# Revit family: pascala_round_901803_004_1_f1d9
name_source: partatom
category: Lighting Fixtures
units: mm (PartAtom-declared; Revit-internal decimal feet)

## family parameters
Cut with Voids When Loaded = No
Host = Face
Light Source = No
Part Type = Normal
Room Calculation Point = No
Round Connector Dimension = Use Diameter
Shared = No

## types (1)
- MultiLumen 1 (1 x LED Modul 940, 1700 lm, 4000)
    Apparent Load = 11 VA
    Approval mark = CE
    CIE Flux Codes = 95 100 100 100 100
    Color Rendering = 92
    Color Temperature = 4000
    Default Elevation = 1800 mm
    Description = Series: PASCALA round
High quality recessed downlight. Mounting bracket: galvanised sheet steel. Inner and closure ring: die-cast aluminium. Brilliantly luminous corona at the light-emitting surfaces thanks to use of a specially designed cast aluminium ring as a reflector closure. Reflector material: MIRO-SILVER with 98 percent total light reflection. Patented round design shaped like a truncated cone. MultiLumen: 16 different luminous fluxes can be set on site in approx. 200 lm steps using DIP switches on the separate converter. Installation without tools thanks to spring fastening system. Converter in separate ballast box with connecting cable plugged in. With connecting cable (L 400 mm). Through-wiring box (5 pole) available as accessory. Possible accessories - please order separately: Extensive selection of accessory covers - can all be retrofitted without tools. IP 54 to be achieved with corresponding accessories. 
Colour: silver, matt (approx. RAL 9006)
Diameter: 241 mm
Height: 2 mm
Cut-out diameter: 228 mm
Recess height: 160 mm
Luminaire: recess height: 156 mm
Lamp: LED
Socket: without socket
Colour temperature: 4000K
Colour rendering index (CRI): 92
System power: 11 W
Rated luminous flux: 1700 lm
Luminous efficiency: 155 lm/W
System power 2: 19 W
Rated luminous flux 2: 2700 lm
Luminous efficiency 2: 142 lm/W
System power 3: 26 W
Rated luminous flux 3: 3600 lm
Luminous efficiency 3: 138 lm/W
System power 4: 39 W
Rated luminous flux 4: 5150 lm
Luminous efficiency 4: 132 lm/W
Control gear: Regulated power supply
Protection class: II
Type of protection: IP 20
    Height = 0 mm  [stored 0 ft]
    Lamp = 1 x LED Modul 940
    Lamp Light Flux = 1700 lm
    Lamp count = 1
    Length = 241 mm
    Lifetime = 50000 h
    Luminous efficacy = 155 lm/W
    Manufacturer = RZB
    ModVariant = No
    Model = 901803.004.1
    Mounting Place = Ceiling
    Mounting Type = Recessed
    Number of Poles = 1
    OnlyDefault = Yes
    Power Factor = 1
    Product Name = PASCALA round
    Product group = Recessed downlights
    ProductGroupID = 402
    Protection Class = Protection class II
    Protection Degree = IP 20
    RLX_Detail_Level = 1
    RLX_Emergency_Light_Flux = 0 lm
    RLX_Emergency_Type = 0
    RLX_Emergency_Type_DB = No
    RlxData = <blob elided: 48677 chars, md5=ed5df95a>
    Socket = socket
    Standby Power = 0 W
    System Light Flux = 1700 lm
    System Power = 11 W
    Type Comments = MultiLumen 1
    Type Image = 901557.004.jpg
    URL = http://relux.com
    VarID = multilumen_1
    Voltage = 230 V
    Voltage Range = 220-240 V
    Weight = 0.00 kg
    Width = 0 mm  [stored 0 ft]

note: [stored X ft] marks values corroborated as IEEE doubles in the binary element streams (Revit-internal decimal feet)

## geometry (parser evidence)
native form markers: Sweep x10
no freeform markers — native parametric forms only
